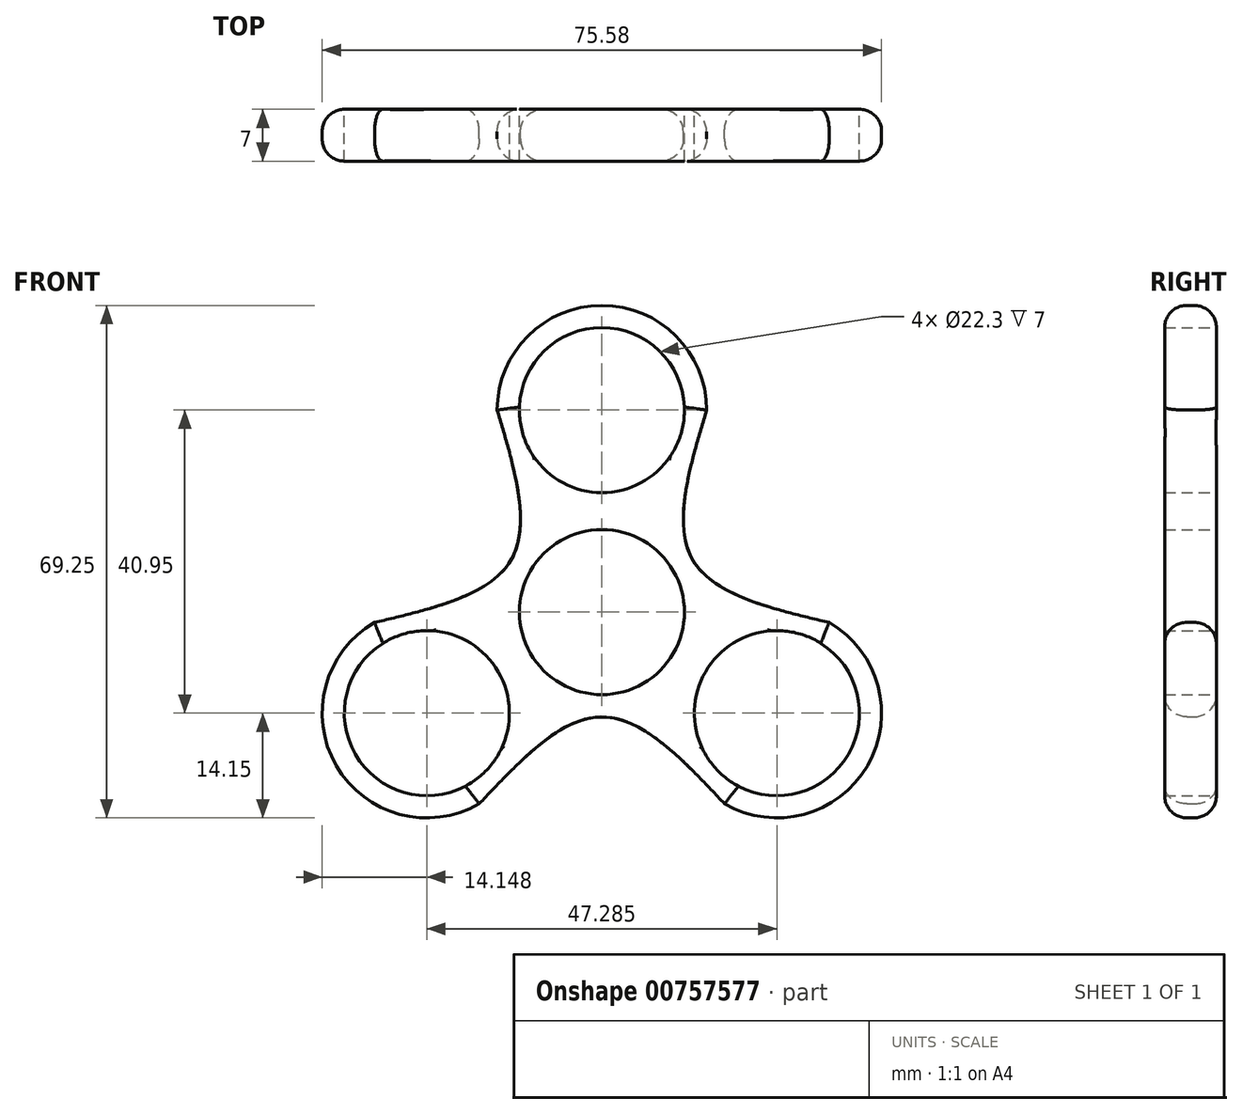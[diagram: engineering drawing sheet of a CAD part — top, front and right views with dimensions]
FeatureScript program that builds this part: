
annotation { "Feature Type Name" : "Feature", "Feature Type Description" : "" }
export const myFeature = defineFeature(function(context is Context, id is Id, definition is map)
    precondition{}
    {
        {
            var Q0;
            Q0=qCreatedBy(makeId("Front.planeOp"),FACE);
            var sketch = newSketch(context, id + "F0", { "sketchPlane" : qUnion([Q0])});
            skCircle(sketch, "E0", {"center": v(0, 0) * mm, "radius": 11.15 * mm});
            skCircle(sketch, "E1", {"center": v(0, 27.3) * mm, "radius": 11.15 * mm});
            skCircle(sketch, "E2.1.0", {"center": v(-23.64, -13.65) * mm, "radius": 11.15 * mm});
            skArc(sketch, "E3.0", {"start": v(12.06, 19.9) * mm, "mid": v(0, 41.45) * mm, "end": v(-12.06, 19.9) * mm});
            skArc(sketch, "E4.0", {"start": v(-23.27, 0.5) * mm, "mid": v(-35.9, -20.72) * mm, "end": v(-11.2, -20.4) * mm});
            skArc(sketch, "E5.0", {"start": v(11.2, -20.4) * mm, "mid": v(35.9, -20.72) * mm, "end": v(23.27, 0.5) * mm});
            skFitSpline(sketch, "E6", {"points": [v(-16.57, -25.9) * mm, v(0, -14.15) * mm, v(16.57, -25.9) * mm], "startDerivative": vector(33.13, 35.26) * mm, "endDerivative": vector(33.13, -35.26) * mm});
            skFitSpline(sketch, "E7", {"points": [v(30.72, -1.4) * mm, v(12.25, 7.07) * mm, v(14.15, 27.3) * mm], "startDerivative": vector(-47.1, 11.06) * mm, "endDerivative": vector(13.97, 46.33) * mm});
            skFitSpline(sketch, "E8", {"points": [v(-14.15, 27.3) * mm, v(-12.25, 7.07) * mm, v(-30.72, -1.4) * mm], "startDerivative": vector(13.97, -46.33) * mm, "endDerivative": vector(-47.1, -11.06) * mm});
            skCircle(sketch, "E9", {"center": v(23.64, -13.65) * mm, "radius": 11.15 * mm});
            skSolve(sketch);
        }
        {
            var Q0;
            Q0=makeQuery(id+"F0.imprint","IMPRINT",FACE,{"disambiguationData":[TD([[makeQuery(id+"F0.imprint","IMPRINT",EDGE,{"derivedFrom":sQuery(id+"F0.wireOp",EDGE,"E0")}),-1.0]])]});
            extrude(context, id + "F1", {"entities" : qUnion([Q0]), "depth" : 7 * mm, "offsetDistance" : 25.4 * mm});
        }
        {
            var Q0;
            Q0=makeQuery(id+"F1.opExtrude","CAP_EDGE",EDGE,{"disambiguationData":[OSD([sQuery(id+"F0.wireOp",EDGE,"E6")])],"isStart":false});
            var Q1;
            Q1=makeQuery(id+"F1.opExtrude","CAP_EDGE",EDGE,{"disambiguationData":[OSD([sQuery(id+"F0.wireOp",EDGE,"E4.0")])],"isStart":false});
            var Q2;
            Q2=makeQuery(id+"F1.opExtrude","CAP_EDGE",EDGE,{"disambiguationData":[OSD([sQuery(id+"F0.wireOp",EDGE,"E8")])],"isStart":false});
            var Q3;
            Q3=makeQuery(id+"F1.opExtrude","CAP_EDGE",EDGE,{"disambiguationData":[OSD([sQuery(id+"F0.wireOp",EDGE,"E3.0")])],"isStart":false});
            var Q4;
            Q4=makeQuery(id+"F1.opExtrude","CAP_EDGE",EDGE,{"disambiguationData":[OSD([sQuery(id+"F0.wireOp",EDGE,"E7")])],"isStart":false});
            var Q5;
            Q5=makeQuery(id+"F1.opExtrude","CAP_EDGE",EDGE,{"disambiguationData":[OSD([sQuery(id+"F0.wireOp",EDGE,"E5.0")])],"isStart":false});
            var Q6;
            Q6=makeQuery(id+"F1.opExtrude","CAP_EDGE",EDGE,{"disambiguationData":[OSD([sQuery(id+"F0.wireOp",EDGE,"E6")])],"isStart":true});
            var Q7;
            Q7=makeQuery(id+"F1.opExtrude","CAP_EDGE",EDGE,{"disambiguationData":[OSD([sQuery(id+"F0.wireOp",EDGE,"E5.0")])],"isStart":true});
            var Q8;
            Q8=makeQuery(id+"F1.opExtrude","CAP_EDGE",EDGE,{"disambiguationData":[OSD([sQuery(id+"F0.wireOp",EDGE,"E7")])],"isStart":true});
            var Q9;
            Q9=makeQuery(id+"F1.opExtrude","CAP_EDGE",EDGE,{"disambiguationData":[OSD([sQuery(id+"F0.wireOp",EDGE,"E4.0")])],"isStart":true});
            var Q10;
            Q10=makeQuery(id+"F1.opExtrude","CAP_EDGE",EDGE,{"disambiguationData":[OSD([sQuery(id+"F0.wireOp",EDGE,"E8")])],"isStart":true});
            var Q11;
            Q11=makeQuery(id+"F1.opExtrude","CAP_EDGE",EDGE,{"disambiguationData":[OSD([sQuery(id+"F0.wireOp",EDGE,"E3.0")])],"isStart":true});
            fillet(context, id + "F2", {"entities" : qUnion([Q0, Q1, Q2, Q3, Q4, Q5, Q6, Q7, Q8, Q9, Q10, Q11]), "radius" : 3 * mm, "tangentPropagation" : true, "allowEdgeOverflow" : false});
        }
    });
